# Revit family: Indoor_Table Lamp_Santa&Cole_Básica Mínima Batería
name_source: partatom
category: Luminarias
revit_build: Autodesk Revit 2018 (Build: 20190510_1515(x64)
units: mm (PartAtom-declared; Revit-internal decimal feet)

## family parameters
Compartido = No
Corte con vacíos al cargar = No
Cota de conector redondo = Diámetro de uso
Número OmniClass = 23.80.70.00
Origen de luz = Sí
Punto de cálculo de habitación = No
Se basa en plano de trabajo = No
Siempre vertical = Sí
Tipo de pieza = Normal
Título OmniClass = Lighting

## types (2) — shared parameters
Archivo de red fotométrica = Básica Mínima Bateria cartulina BAMBTA01 (CL004A21F002G).IES
Assembly instructions - CE = https://www.santacole.com
Cambio de temperatura de color de luz atenuada = <Ninguno>
Carga aparente = 17 VA
Code = BABTA01
Fabricante = Santa & Cole
Filtro de color = 16777215
Load = 17 W
Manufacturer website = http://www.santacole.com
Modelo = Básica Mínima Batería
Technical Information = https://www.santacole.com
URL = https://www.santacole.com
Ángulo de inclinación = 90.00°

## per-type parameters (varying)
| type | Lampshade Material | Visibility_Beige Parchment |
| Pleated natural parchment | Santa & Cole - Beige Cardboard | Sí |
| Ribbon stitched | Santa & Cole - Natural Ribbon | No |

## geometry (parser evidence)
native form markers: Sweep x1
no freeform markers — native parametric forms only
